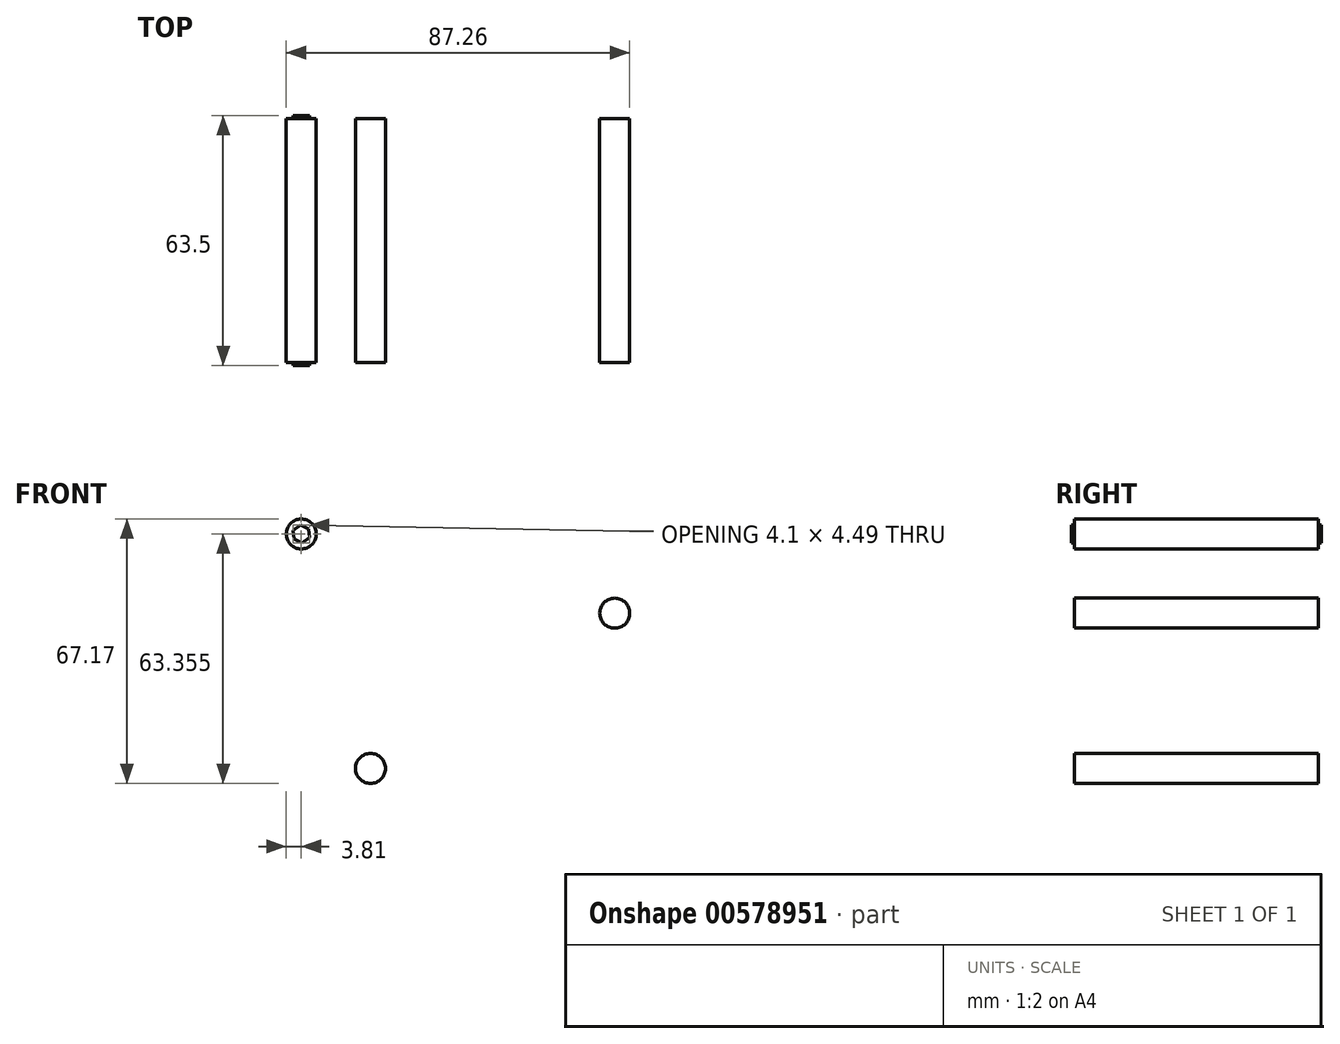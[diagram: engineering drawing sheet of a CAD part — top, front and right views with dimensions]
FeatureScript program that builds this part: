
annotation { "Feature Type Name" : "Feature", "Feature Type Description" : "" }
export const myFeature = defineFeature(function(context is Context, id is Id, definition is map)
    precondition{}
    {
        {
            var Q0;
            Q0=qCreatedBy(makeId("Front.planeOp"),FACE);
            var sketch = newSketch(context, id + "F0", { "sketchPlane" : qUnion([Q0])});
            skCircle(sketch, "E0", {"center": v(30.8, 25.33) * mm, "radius": 3.81 * mm});
            skCircle(sketch, "E1", {"center": v(-48.84, 45.45) * mm, "radius": 3.81 * mm});
            skCircle(sketch, "E2", {"center": v(-31.26, -14.1) * mm, "radius": 3.81 * mm});
            skSolve(sketch);
        }
        {
            var Q0;
            Q0 = qSketchRegion(id + "F0", true);
            extrude(context, id + "F1", {"entities" : qUnion([Q0]), "depth" : 30.99 * mm, "offsetDistance" : 25.4 * mm, "hasSecondDirection" : true, "secondDirectionOppositeDirection" : true, "secondDirectionDepth" : 30.99 * mm});
        }
        {
            var Q0;
            Q0=makeQuery(id+"F1.opExtrude","CAP_FACE",FACE,{"disambiguationData":[OSD([sQuery(id+"F0.wireOp",EDGE,"E1")])],"isStart":false});
            var sketch = newSketch(context, id + "F2", { "sketchPlane" : qUnion([Q0])});
            skCircle(sketch, "E3.cCircle", {"center": v(-48.84, 45.45) * mm, "radius": 1.95 * mm, "construction": true});
            skLineSegment(sketch, "E3.0", {"start": v(-48.62, 43.2) * mm, "end": v(-50.68, 44.14) * mm});
            skLineSegment(sketch, "E3.1", {"start": v(-50.68, 44.14) * mm, "end": v(-50.9, 46.38) * mm});
            skLineSegment(sketch, "E3.2", {"start": v(-50.9, 46.38) * mm, "end": v(-49.06, 47.69) * mm});
            skLineSegment(sketch, "E3.3", {"start": v(-49.06, 47.69) * mm, "end": v(-47, 46.75) * mm});
            skLineSegment(sketch, "E3.4", {"start": v(-47, 46.75) * mm, "end": v(-46.79, 44.51) * mm});
            skLineSegment(sketch, "E3.5", {"start": v(-46.79, 44.51) * mm, "end": v(-48.62, 43.2) * mm});
            skPoint(sketch, "E3.0.midPoint", {"position": v(-49.65, 43.67) * mm});
            skSolve(sketch);
        }
        {
            var Q0;
            Q0=makeQuery(id+"F2.imprint","IMPRINT",FACE,{"disambiguationData":[TD([[makeQuery(id+"F2.imprint","IMPRINT",EDGE,{"derivedFrom":sQuery(id+"F2.wireOp",EDGE,"E3.0")}),-1.0]])]});
            extrude(context, id + "F3", {"entities" : qUnion([Q0]), "operationType" : NewBodyOperationType.ADD, "depth" : 0.76 * mm, "offsetDistance" : 25.4 * mm, "hasSecondDirection" : true, "secondDirectionOppositeDirection" : true, "secondDirectionDepth" : 62.74 * mm});
        }
    });
